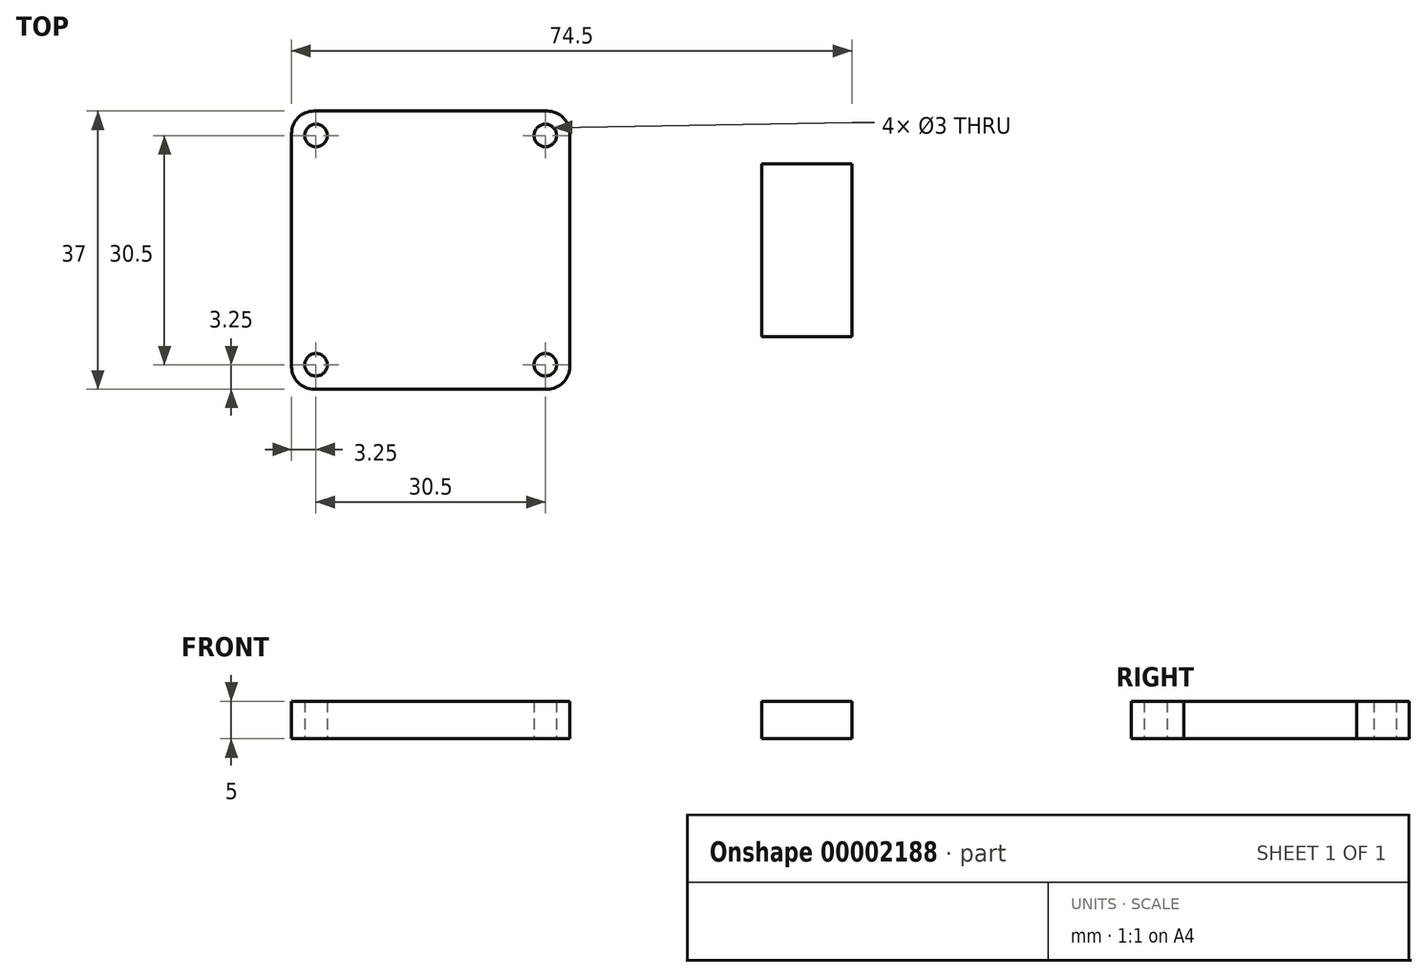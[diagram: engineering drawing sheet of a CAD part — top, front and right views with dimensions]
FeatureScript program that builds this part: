
annotation { "Feature Type Name" : "Feature", "Feature Type Description" : "" }
export const myFeature = defineFeature(function(context is Context, id is Id, definition is map)
    precondition{}
    {
        {
            var Q0;
            Q0=qCreatedBy(makeId("Top.planeOp"),FACE);
            var sketch = newSketch(context, id + "F0", { "sketchPlane" : qUnion([Q0])});
            skLineSegment(sketch, "E0.rect.bottom", {"start": v(15.5, -18.5) * mm, "end": v(-15.5, -18.5) * mm});
            skLineSegment(sketch, "E0.rect.top", {"start": v(15.5, 18.5) * mm, "end": v(-15.5, 18.5) * mm});
            skLineSegment(sketch, "E0.rect.left", {"start": v(18.5, -15.5) * mm, "end": v(18.5, 15.5) * mm});
            skLineSegment(sketch, "E0.rect.right", {"start": v(-18.5, -15.5) * mm, "end": v(-18.5, 15.5) * mm});
            skPoint(sketch, "E0.rect.middle", {"position": v(0, 0) * mm});
            skLineSegment(sketch, "E1.rect.bottom", {"start": v(15.25, -15.25) * mm, "end": v(-15.25, -15.25) * mm, "construction": true});
            skLineSegment(sketch, "E1.rect.top", {"start": v(15.25, 15.25) * mm, "end": v(-15.25, 15.25) * mm, "construction": true});
            skLineSegment(sketch, "E1.rect.left", {"start": v(15.25, -15.25) * mm, "end": v(15.25, 15.25) * mm, "construction": true});
            skLineSegment(sketch, "E1.rect.right", {"start": v(-15.25, -15.25) * mm, "end": v(-15.25, 15.25) * mm, "construction": true});
            skCircle(sketch, "E2", {"center": v(-15.25, 15.25) * mm, "radius": 1.5 * mm});
            skCircle(sketch, "E3", {"center": v(15.25, 15.25) * mm, "radius": 1.5 * mm});
            skCircle(sketch, "E4", {"center": v(15.25, -15.25) * mm, "radius": 1.5 * mm});
            skCircle(sketch, "E5", {"center": v(-15.25, -15.25) * mm, "radius": 1.5 * mm});
            skPoint(sketch, "E6.visualSharp", {"position": v(18.5, 18.5) * mm});
            skArc(sketch, "E6.filletArc", {"start": v(18.5, 15.5) * mm, "mid": v(17.62, 17.62) * mm, "end": v(15.5, 18.5) * mm});
            skPoint(sketch, "E7.visualSharp", {"position": v(18.5, -18.5) * mm});
            skArc(sketch, "E7.filletArc", {"start": v(15.5, -18.5) * mm, "mid": v(17.62, -17.62) * mm, "end": v(18.5, -15.5) * mm});
            skPoint(sketch, "E8.visualSharp", {"position": v(-18.5, -18.5) * mm});
            skArc(sketch, "E8.filletArc", {"start": v(-18.5, -15.5) * mm, "mid": v(-17.62, -17.62) * mm, "end": v(-15.5, -18.5) * mm});
            skPoint(sketch, "E9.visualSharp", {"position": v(-18.5, 18.5) * mm});
            skArc(sketch, "E9.filletArc", {"start": v(-15.5, 18.5) * mm, "mid": v(-17.62, 17.62) * mm, "end": v(-18.5, 15.5) * mm});
            skSolve(sketch);
        }
        {
            var Q0;
            Q0=qSketchRegion(id+"F0",true);
            extrude(context, id + "F1", {"entities" : qUnion([Q0]), "depth" : 5 * mm});
        }
        {
            var Q0;
            Q0=qCreatedBy(makeId("Top.planeOp"),FACE);
            var sketch = newSketch(context, id + "F2", { "sketchPlane" : qUnion([Q0])});
            skLineSegment(sketch, "E10.rect.bottom", {"start": v(56, -11.5) * mm, "end": v(44, -11.5) * mm});
            skLineSegment(sketch, "E10.rect.top", {"start": v(56, 11.5) * mm, "end": v(44, 11.5) * mm});
            skLineSegment(sketch, "E10.rect.left", {"start": v(56, -11.5) * mm, "end": v(56, 11.5) * mm});
            skLineSegment(sketch, "E10.rect.right", {"start": v(44, -11.5) * mm, "end": v(44, 11.5) * mm});
            skPoint(sketch, "E10.rect.middle", {"position": v(50, 0) * mm});
            skSolve(sketch);
        }
        {
            var Q0;
            Q0=makeQuery(id+"F2.imprint","IMPRINT",FACE,{"disambiguationData":[TD([[makeQuery(id+"F2.imprint","IMPRINT",EDGE,{"derivedFrom":sQuery(id+"F2.wireOp",EDGE,"E10.rect.bottom")}),-1.0]])]});
            extrude(context, id + "F3", {"entities" : qUnion([Q0]), "depth" : 5 * mm});
        }
    });
